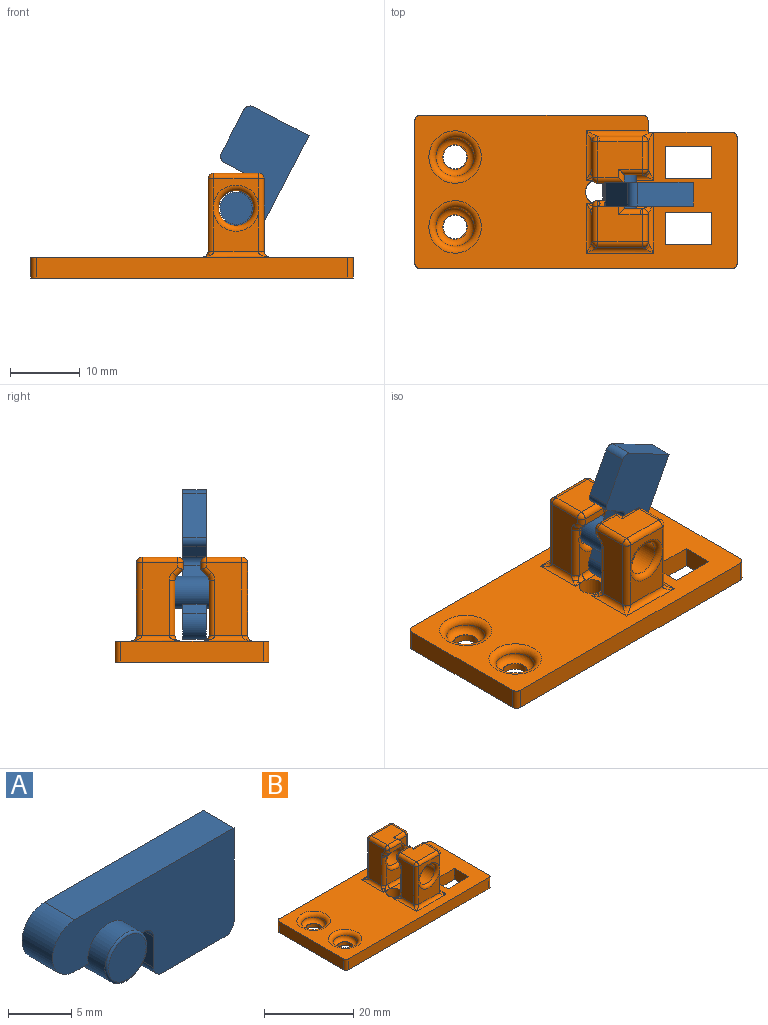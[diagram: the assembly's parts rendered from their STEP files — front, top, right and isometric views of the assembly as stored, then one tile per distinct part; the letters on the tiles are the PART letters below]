
ASSEMBLY  parts=2 mates=1
PART A: 16 faces, bbox 20.3x7x10 mm
  f0: plane 3.4x1.76mm, normal (0,0,-1), area 6mm2, adj f2,f6,f7,f14
  f1: plane 3.4x1.51mm, normal (0,0,-1), area 5.1mm2, adj f2,f4,f6,f7
  f2: plane 20.25x10mm, normal (0,-1,0), area 132.8mm2, adj f0,f1,f3,f4,f5,f7,f10,f11
  f3: plane 17.75x3.4mm, normal (0,0,1), area 60.4mm2, adj f2,f4,f6,f11
  f4: cylinder r=2.5mm len=5mm, axis (0,1,0), area 26.7mm2, adj f1,f2,f3,f6
  f5: plane 3.4x3mm, normal (-1,0,0), area 10.2mm2, adj f2,f6,f13,f14
  f6: plane 20.25x10mm, normal (0,1,0), area 132.8mm2, adj f0,f1,f3,f4,f5,f7,f10,f11
  f7: cylinder r=2.3mm len=6.8mm, axis (0,-1,0), area 70.3mm2, adj f0,f1,f2,f6,f8,f15
  f8: plane 4.6x4.6mm, normal (0,1,0), area 16.6mm2, adj f7
  f9: plane 4.2x4.2mm, normal (0,-1,0), area 13.9mm2, adj f15
  f10: plane 7x3.4mm, normal (0,0,-1), area 23.8mm2, adj f2,f6,f12,f13
  f11: plane 9x3.4mm, normal (1,0,0), area 30.6mm2, adj f2,f3,f6,f12
  f12: cylinder r=1mm len=3.4mm, axis (0,-1,0), area 5.3mm2, adj f2,f6,f10,f11
  f13: cylinder r=1mm len=3.4mm, axis (0,-1,0), area 5.3mm2, adj f2,f5,f6,f10
  f14: cylinder r=1mm len=3.4mm, axis (0,1,0), area 5.3mm2, adj f0,f2,f5,f6
  f15: torus R=2.1mm, axis (0,1,0), area 4.4mm2, adj f7,f9
PART B: 122 faces, bbox 46.2x22.1x15.1 mm
  f0: cylinder r=1.7mm len=3.4mm, axis (0,0,1), area 10.7mm2, adj f10,f117
  f1: cylinder r=1.7mm len=3.4mm, axis (0,0,1), area 10.7mm2, adj f10,f116
  f2: plane 6.4x5.39mm, normal (0,1,0), area 22.7mm2, adj f54,f56,f57,f61
  f3: plane 6.4x5.39mm, normal (0,-1,0), area 22.7mm2, adj f47,f85,f86,f87
  f4: plane 0.86x0.35mm, normal (0,-1,0), area 0.1mm2, adj f74,f78,f79
  f5: plane 6.4x5.4mm, normal (0,-1,0), area 22.7mm2, adj f49,f50,f76,f78,f79,f80
  f6: plane 6.4x5.4mm, normal (0,1,0), area 22.7mm2, adj f43,f44,f101,f105,f108,f110
  f7: plane 0.86x0.35mm, normal (0,1,0), area 0.1mm2, adj f103,f105,f108
  f8: plane 46.1x22mm, normal (0,0,1), area 687.8mm2, adj f9,f11,f12,f13,f14,f15,f16,f17
  f9: plane 31.75x3mm, normal (0,1,0), area 95.2mm2, adj f8,f10,f112,f114
  f10: plane 46.1x22mm, normal (0,0,-1), area 894mm2, adj f0,f1,f9,f11,f12,f13,f14,f15
  f11: plane 44.5x3mm, normal (0,-1,0), area 133.5mm2, adj f8,f10,f113,f115
  f12: plane 17.97x3mm, normal (1,0,0), area 53.9mm2, adj f8,f10,f111,f115
  f13: plane 6.6x3mm, normal (0,-1,0), area 19.8mm2, adj f8,f10,f14,f19
  f14: plane 4.6x3mm, normal (-1,0,0), area 13.8mm2, adj f8,f10,f13,f15
  f15: plane 6.6x3mm, normal (0,1,0), area 19.8mm2, adj f8,f10,f14,f19
  f16: plane 6.6x3mm, normal (0,-1,0), area 19.8mm2, adj f8,f10,f17,f20
  f17: plane 4.6x3mm, normal (-1,0,0), area 13.8mm2, adj f8,f10,f16,f18
  f18: plane 6.6x3mm, normal (0,1,0), area 19.8mm2, adj f8,f10,f17,f20
  f19: plane 4.6x3mm, normal (1,0,0), area 13.8mm2, adj f8,f10,f13,f15
  f20: plane 4.6x3mm, normal (1,0,0), area 13.8mm2, adj f8,f10,f16,f18
  f21: plane 20.4x3mm, normal (-1,0,0), area 61.2mm2, adj f8,f10,f113,f114
  f22: plane 10.4x3.9mm, normal (1,0,0), area 40.6mm2, adj f52,f61,f68,f76
  f23: plane 6.4x3.39mm, normal (0,1,0), area 9.9mm2, adj f56,f57,f60,f61
  f24: plane 10.4x5.1mm, normal (-1,0,0), area 42.1mm2, adj f53,f56,f62,f69,f73,f77,f79
  f25: plane 3.39x2.71mm, normal (0,-1,0), area 4.4mm2, adj f35,f64,f67,f76,f78
  f26: plane 6.4x5.1mm, normal (0,0,1), area 28.6mm2, adj f60,f62,f63,f64,f67,f68
  f27: plane 10.4x3.9mm, normal (1,0,0), area 40.6mm2, adj f45,f87,f94,f101
  f28: plane 3.39x2.71mm, normal (0,1,0), area 4.4mm2, adj f37,f91,f95,f101,f105
  f29: plane 10.4x5.1mm, normal (-1,0,0), area 42.1mm2, adj f48,f86,f93,f100,f104,f106,f108
  f30: plane 6.4x3.39mm, normal (0,-1,0), area 9.9mm2, adj f85,f86,f87,f88
  f31: plane 6.4x5.1mm, normal (0,0,1), area 28.6mm2, adj f88,f91,f92,f93,f94,f95
  f32: cylinder r=2.5mm len=5mm, axis (0,1,0), area 62.8mm2, adj f37,f85,f99,f102,f105
  f33: cylinder r=2.5mm len=5mm, axis (0,1,0), area 62.8mm2, adj f35,f57,f70,f75,f78
  f34: cylinder r=1.75mm len=3.5mm, axis (0,0,1), area 33mm2, adj f8,f10,f44,f49
  f35: plane 2.02x1.65mm, normal (0.99,0,-0.12), area 1.8mm2, adj f25,f33,f36,f39,f64,f70,f78
  f36: plane 3.8x1mm, normal (0,-1,0), area 3.7mm2, adj f35,f39,f63,f64,f69
  f37: plane 2.02x1.65mm, normal (0.99,0,-0.12), area 1.8mm2, adj f28,f32,f38,f40,f91,f99,f105
  f38: plane 3.8x1mm, normal (0,1,0), area 3.7mm2, adj f37,f40,f91,f92,f100
  f39: plane 3.68x0.97mm, normal (0,-0.71,-0.71), area 3.8mm2, adj f35,f36,f70,f73,f74
  f40: plane 3.68x0.97mm, normal (0,0.71,-0.71), area 3.8mm2, adj f37,f38,f99,f103,f104
  f41: plane 12.01x3.08mm, normal (0,1,0), area 35.9mm2, adj f8,f10,f42,f52,f54,f58,f111
  f42: plane 3.02x1.63mm, normal (1,0,0), area 4.9mm2, adj f8,f10,f41,f54,f112
  f43: cylinder r=0.8mm len=7.42mm, axis (-1,0,0), area 8.3mm2, adj f6,f8,f44,f97
  f44: bspline ~1.45x0.86mm, area 1.2mm2, adj f6,f34,f43,f46,f109
  f45: cylinder r=0.8mm len=7.1mm, axis (0,1,0), area 6.9mm2, adj f8,f27,f84,f97
  f46: cylinder r=0.8mm len=1.02mm, axis (-1,0,0), area 0.3mm2, adj f8,f44,f107
  f47: cylinder r=0.8mm len=9.6mm, axis (1,0,0), area 10.1mm2, adj f3,f8,f83,f84
  f48: cylinder r=0.8mm len=7.1mm, axis (0,-1,0), area 6.4mm2, adj f8,f29,f83,f107,f109,f110
  f49: bspline ~1.45x0.86mm, area 1.2mm2, adj f5,f34,f50,f51,f81
  f50: cylinder r=0.8mm len=7.42mm, axis (1,0,0), area 8.3mm2, adj f5,f8,f49,f72
  f51: cylinder r=0.8mm len=1.02mm, axis (1,0,0), area 0.3mm2, adj f8,f49,f82
  f52: cylinder r=0.8mm len=6.92mm, axis (0,1,0), area 6.4mm2, adj f8,f22,f41,f58,f72
  f53: cylinder r=0.8mm len=7.1mm, axis (0,-1,0), area 6.4mm2, adj f8,f24,f55,f80,f81,f82
  f54: cylinder r=0.8mm len=9.24mm, axis (-1,0,0), area 9.4mm2, adj f2,f8,f41,f42,f55,f58
  f55: bspline ~1.6x1.6mm, area 0.7mm2, adj f53,f54,f56
  f56: cylinder r=0.8mm len=10.4mm, axis (0,0,-1), area 13mm2, adj f2,f23,f24,f55,f57,f59
  f57: torus R=3.3mm, axis (0,-1,0), area 21.9mm2, adj f2,f23,f33,f56,f61
  f58: bspline ~1.55x1.55mm, area 1.2mm2, adj f41,f52,f54,f61
  f59: sphere r=0.8mm, area 1.4mm2, adj f56,f60,f62
  f60: cylinder r=0.8mm len=6.4mm, axis (1,0,0), area 8mm2, adj f23,f26,f59,f65
  f61: cylinder r=0.8mm len=10.4mm, axis (0,0,1), area 13mm2, adj f2,f22,f23,f57,f58,f65
  f62: cylinder r=0.8mm len=5.1mm, axis (0,1,0), area 6.4mm2, adj f24,f26,f59,f66
  f63: cylinder r=0.8mm len=3.8mm, axis (-1,0,0), area 4.3mm2, adj f26,f36,f64,f66
  f64: cylinder r=0.8mm len=2mm, axis (0,1,0), area 1.6mm2, adj f25,f26,f35,f36,f63,f67
  f65: sphere r=0.8mm, area 0.6mm2, adj f60,f61,f68
  f66: sphere r=0.8mm, area 1mm2, adj f62,f63,f69
  f67: cylinder r=0.8mm len=3.4mm, axis (-1,0,0), area 3.8mm2, adj f25,f26,f64,f71
  f68: cylinder r=0.8mm len=3.9mm, axis (0,-1,0), area 4.9mm2, adj f22,f26,f65,f71
  f69: cylinder r=0.8mm len=1mm, axis (0,0,1), area 1mm2, adj f24,f36,f66,f73
  f70: bspline ~2.26x1.07mm, area 1.4mm2, adj f33,f35,f39,f75
  f71: sphere r=0.8mm, area 1mm2, adj f67,f68,f76
  f72: bspline ~1.6x1.6mm, area 0.7mm2, adj f50,f52,f76
  f73: cylinder r=0.8mm len=1.53mm, axis (0,0.71,-0.71), area 1.5mm2, adj f24,f39,f69,f77
  f74: cylinder r=0.8mm len=1.45mm, axis (-1,0,0), area 0.6mm2, adj f4,f39,f75,f77
  f75: bspline ~1.84x1.16mm, area 1.2mm2, adj f33,f70,f74,f78
  f76: cylinder r=0.8mm len=10.4mm, axis (0,0,-1), area 13mm2, adj f5,f22,f25,f71,f72,f78
  f77: torus R=1.6mm, axis (1,0,0), area 1.1mm2, adj f24,f73,f74,f79
  f78: torus R=3.3mm, axis (0,-1,0), area 17.7mm2, adj f4,f5,f25,f33,f35,f75,f76,f79
  f79: cylinder r=0.8mm len=7.87mm, axis (0,0,1), area 9.8mm2, adj f4,f5,f24,f77,f78,f80
  f80: torus R=1.6mm, axis (0,-1,0), area 0mm2, adj f5,f53,f79,f81
  f81: bspline ~1.14x1.14mm, area 0.8mm2, adj f49,f53,f80,f82
  f82: bspline ~1.17x1.17mm, area 0.3mm2, adj f51,f53,f81
  f83: bspline ~1.6x1.6mm, area 0.7mm2, adj f47,f48,f86
  f84: bspline ~1.6x1.6mm, area 0.7mm2, adj f45,f47,f87
  f85: torus R=3.3mm, axis (0,-1,0), area 21.9mm2, adj f3,f30,f32,f86,f87
  f86: cylinder r=0.8mm len=10.4mm, axis (0,0,1), area 13mm2, adj f3,f29,f30,f83,f85,f89
  f87: cylinder r=0.8mm len=10.4mm, axis (0,0,-1), area 13mm2, adj f3,f27,f30,f84,f85,f90
  f88: cylinder r=0.8mm len=6.4mm, axis (-1,0,0), area 8mm2, adj f30,f31,f89,f90
  f89: sphere r=0.8mm, area 1mm2, adj f86,f88,f93
  f90: sphere r=0.8mm, area 1mm2, adj f87,f88,f94
  f91: cylinder r=0.8mm len=2mm, axis (0,1,0), area 1.6mm2, adj f28,f31,f37,f38,f92,f95
  f92: cylinder r=0.8mm len=3.8mm, axis (-1,0,0), area 4.3mm2, adj f31,f38,f91,f96
  f93: cylinder r=0.8mm len=5.1mm, axis (0,1,0), area 6.4mm2, adj f29,f31,f89,f96
  f94: cylinder r=0.8mm len=3.9mm, axis (0,-1,0), area 4.9mm2, adj f27,f31,f90,f98
  f95: cylinder r=0.8mm len=3.4mm, axis (1,0,0), area 3.8mm2, adj f28,f31,f91,f98
  f96: sphere r=0.8mm, area 1.4mm2, adj f92,f93,f100
  f97: bspline ~1.6x1.6mm, area 0.7mm2, adj f43,f45,f101
  f98: sphere r=0.8mm, area 1.4mm2, adj f94,f95,f101
  f99: bspline ~2.26x1.07mm, area 1.4mm2, adj f32,f37,f40,f102
  f100: cylinder r=0.8mm len=1mm, axis (0,0,1), area 1mm2, adj f29,f38,f96,f104
  f101: cylinder r=0.8mm len=10.4mm, axis (0,0,1), area 13mm2, adj f6,f27,f28,f97,f98,f105
  f102: bspline ~1.83x1.28mm, area 1.2mm2, adj f32,f99,f103,f105
  f103: cylinder r=0.8mm len=1.45mm, axis (-1,0,0), area 0.6mm2, adj f7,f40,f102,f106
  f104: cylinder r=0.8mm len=1.53mm, axis (0,-0.71,-0.71), area 1.5mm2, adj f29,f40,f100,f106
  f105: torus R=3.3mm, axis (0,-1,0), area 17.7mm2, adj f6,f7,f28,f32,f37,f101,f102,f108
  f106: torus R=1.6mm, axis (1,0,0), area 1.1mm2, adj f29,f103,f104,f108
  f107: bspline ~1.17x1.17mm, area 0.3mm2, adj f46,f48,f109
  f108: cylinder r=0.8mm len=7.87mm, axis (0,0,-1), area 9.8mm2, adj f6,f7,f29,f105,f106,f110
  f109: bspline ~1.14x1.13mm, area 0.8mm2, adj f44,f48,f107,f110
  f110: torus R=1.6mm, axis (0,-1,0), area 0mm2, adj f6,f48,f108,f109
  f111: cylinder r=0.8mm len=3mm, axis (0,0,-1), area 3.8mm2, adj f8,f10,f12,f41
  f112: cylinder r=0.8mm len=3mm, axis (0,0,1), area 3.8mm2, adj f8,f9,f10,f42
  f113: cylinder r=0.8mm len=3mm, axis (0,0,-1), area 3.8mm2, adj f8,f10,f11,f21
  f114: cylinder r=0.8mm len=3mm, axis (0,0,1), area 3.8mm2, adj f8,f9,f10,f21
  f115: cylinder r=0.8mm len=3mm, axis (0,0,1), area 3.8mm2, adj f8,f10,f11,f12
  f116: plane 3.5x3.5mm, normal (0,0,1), area 0.5mm2, adj f1,f120
  f117: plane 3.5x3.5mm, normal (0,0,1), area 0.5mm2, adj f0,f118
  f118: torus R=1.75mm, axis (0,0,1), area 23.6mm2, adj f117,f119
  f119: torus R=3.75mm, axis (0,0,1), area 30.7mm2, adj f8,f118
  f120: torus R=1.75mm, axis (0,0,1), area 23.6mm2, adj f116,f121
  f121: torus R=3.75mm, axis (0,0,1), area 30.7mm2, adj f8,f120
PLACE A rot(axis=(0.86,0,0.52),180deg) t=(-16.71,3.13,20.26)mm
PLACE B rot(axis=(-0.22,0.19,-0.96),0deg) t=(-3.56,3.23,-0.53)mm fixed
MATE revolute B.f32 <-> A.f15  axis (0,-1,0) through (-13.31,5.68,9.47)mm
